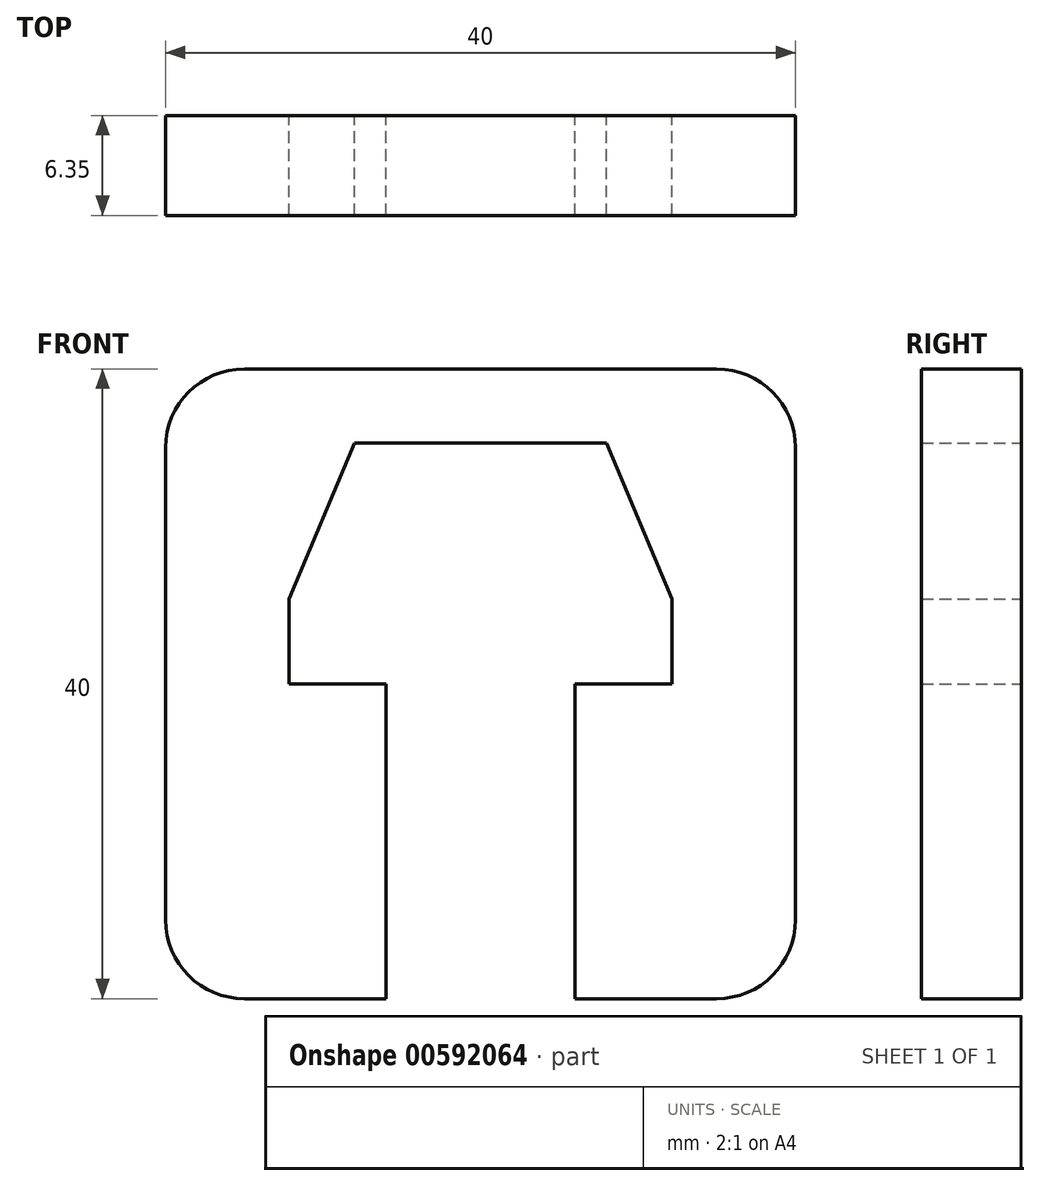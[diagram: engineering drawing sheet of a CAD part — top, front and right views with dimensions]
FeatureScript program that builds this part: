
annotation { "Feature Type Name" : "Feature", "Feature Type Description" : "" }
export const myFeature = defineFeature(function(context is Context, id is Id, definition is map)
    precondition{}
    {
        {
            var Q0;
            Q0=qCreatedBy(makeId("Front.planeOp"),FACE);
            var sketch = newSketch(context, id + "F0", { "sketchPlane" : qUnion([Q0])});
            skLineSegment(sketch, "E0", {"start": v(0, -10) * mm, "end": v(0, -50) * mm, "construction": true});
            skLineSegment(sketch, "E1", {"start": v(-8, -14.7) * mm, "end": v(8, -14.7) * mm});
            skLineSegment(sketch, "E2", {"start": v(8, -14.7) * mm, "end": v(12.15, -24.6) * mm});
            skLineSegment(sketch, "E3", {"start": v(12.15, -24.6) * mm, "end": v(12.15, -30) * mm});
            skLineSegment(sketch, "E4", {"start": v(12.15, -30) * mm, "end": v(6, -30) * mm});
            skLineSegment(sketch, "E5", {"start": v(-12.15, -30) * mm, "end": v(-12.15, -24.6) * mm});
            skLineSegment(sketch, "E6", {"start": v(-12.15, -24.6) * mm, "end": v(-8, -14.7) * mm});
            skPoint(sketch, "E7", {"position": v(0, -14.7) * mm});
            skPoint(sketch, "E8", {"position": v(0, -30) * mm});
            skLineSegment(sketch, "E9", {"start": v(6, -30) * mm, "end": v(6, -50) * mm});
            skLineSegment(sketch, "E10.MirrorCS", {"start": v(-6, -30) * mm, "end": v(-6, -50) * mm});
            skLineSegment(sketch, "E11.trimOffspring", {"start": v(-6, -30) * mm, "end": v(-12.15, -30) * mm});
            skLineSegment(sketch, "E12.bottom", {"start": v(-15, -10) * mm, "end": v(15, -10) * mm});
            skLineSegment(sketch, "E12.top", {"start": v(-15, -50) * mm, "end": v(-6, -50) * mm});
            skLineSegment(sketch, "E12.left", {"start": v(-20, -15) * mm, "end": v(-20, -45) * mm});
            skLineSegment(sketch, "E12.right", {"start": v(20, -15) * mm, "end": v(20, -45) * mm});
            skPoint(sketch, "E13.visualSharp", {"position": v(-20, -10) * mm});
            skArc(sketch, "E13.filletArc", {"start": v(-15, -10) * mm, "mid": v(-18.54, -11.46) * mm, "end": v(-20, -15) * mm});
            skPoint(sketch, "E14.visualSharp", {"position": v(20, -10) * mm});
            skArc(sketch, "E14.filletArc", {"start": v(20, -15) * mm, "mid": v(18.54, -11.46) * mm, "end": v(15, -10) * mm});
            skPoint(sketch, "E15.visualSharp", {"position": v(20, -50) * mm});
            skArc(sketch, "E15.filletArc", {"start": v(15, -50) * mm, "mid": v(18.54, -48.54) * mm, "end": v(20, -45) * mm});
            skPoint(sketch, "E16.visualSharp", {"position": v(-20, -50) * mm});
            skArc(sketch, "E16.filletArc", {"start": v(-20, -45) * mm, "mid": v(-18.54, -48.54) * mm, "end": v(-15, -50) * mm});
            skLineSegment(sketch, "E17.trimOffspring", {"start": v(6, -50) * mm, "end": v(15, -50) * mm});
            skSolve(sketch);
        }
        {
            var Q0;
            Q0=qSketchRegion(id+"F0",true);
            extrude(context, id + "F1", {"entities" : qUnion([Q0]), "depth" : 6.35 * mm, "offsetDistance" : 25 * mm});
        }
    });
